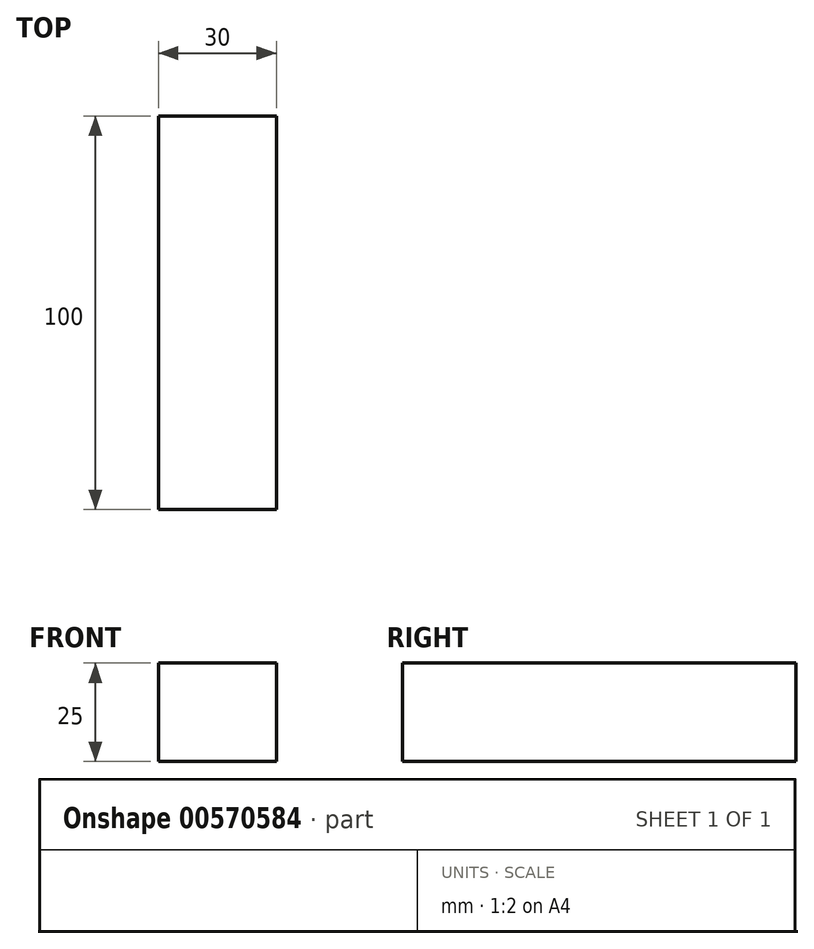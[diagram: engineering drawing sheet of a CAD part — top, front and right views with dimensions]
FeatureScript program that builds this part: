
annotation { "Feature Type Name" : "Feature", "Feature Type Description" : "" }
export const myFeature = defineFeature(function(context is Context, id is Id, definition is map)
    precondition{}
    {
        {
            var Q0;
            Q0=qCreatedBy(makeId("Top.planeOp"),FACE);
            var sketch = newSketch(context, id + "F0", { "sketchPlane" : qUnion([Q0])});
            skLineSegment(sketch, "E0.bottom", {"start": v(15, -52.29) * mm, "end": v(-15, -52.29) * mm});
            skLineSegment(sketch, "E0.top", {"start": v(15, 47.71) * mm, "end": v(-15, 47.71) * mm});
            skLineSegment(sketch, "E0.left", {"start": v(15, -52.29) * mm, "end": v(15, 47.71) * mm});
            skLineSegment(sketch, "E0.right", {"start": v(-15, -52.29) * mm, "end": v(-15, 47.71) * mm});
            skPoint(sketch, "E0.middle", {"position": v(0, -2.29) * mm});
            skSolve(sketch);
        }
        {
            var Q0;
            Q0 = qSketchRegion(id + "F0", true);
            extrude(context, id + "F1", {"entities" : qUnion([Q0]), "depth" : 25 * mm, "offsetDistance" : 25 * mm});
        }
    });
